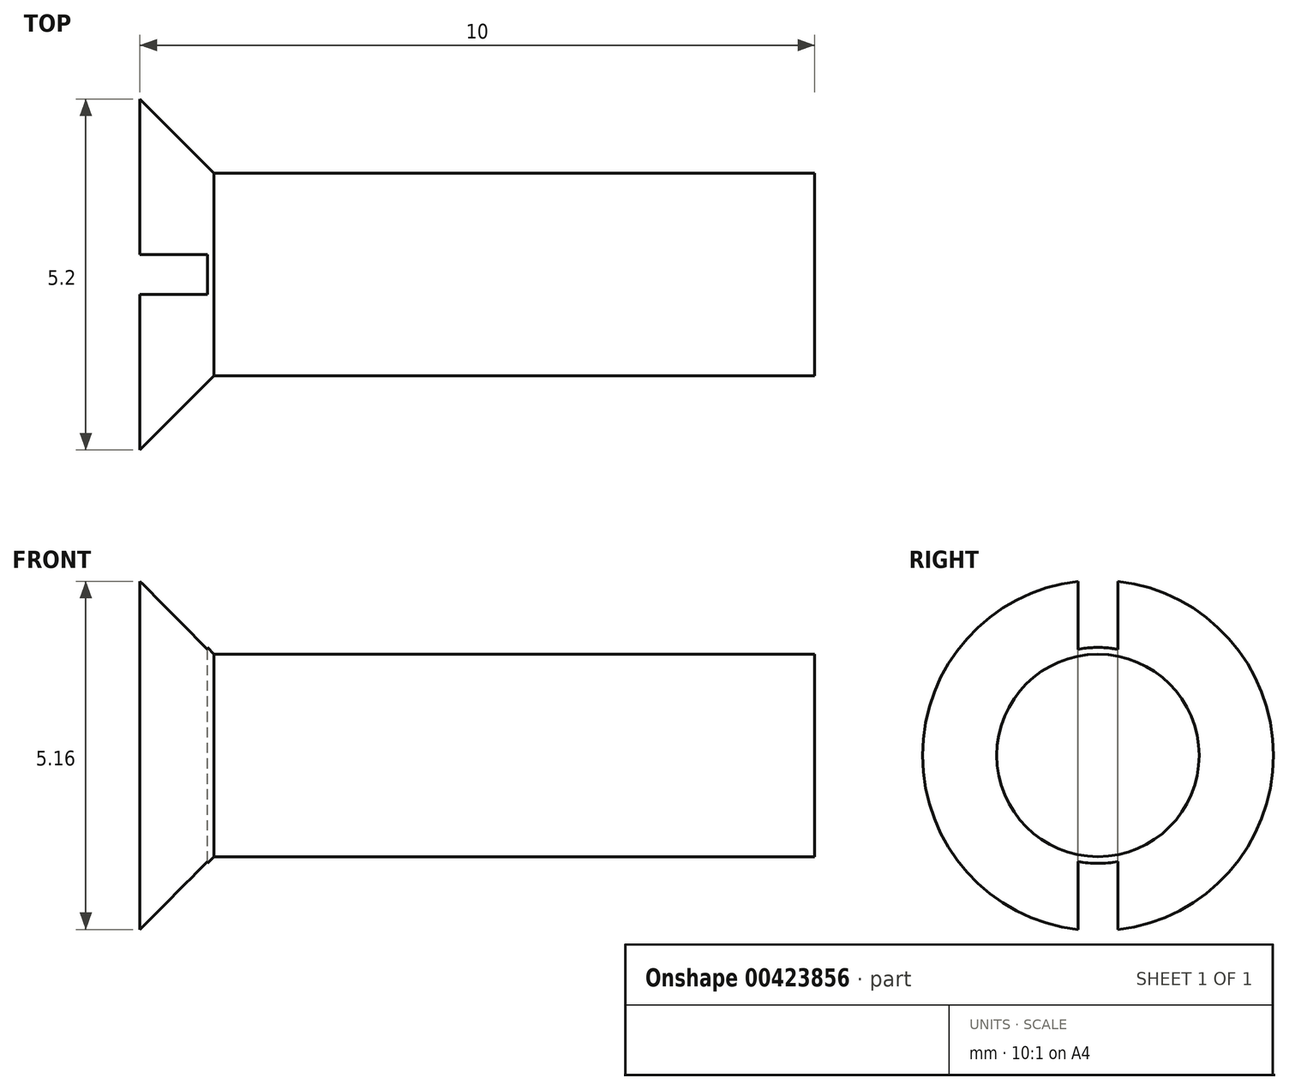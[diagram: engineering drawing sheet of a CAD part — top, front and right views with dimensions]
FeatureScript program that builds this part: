
annotation { "Feature Type Name" : "Feature", "Feature Type Description" : "" }
export const myFeature = defineFeature(function(context is Context, id is Id, definition is map)
    precondition{}
    {
        {
            var Q0;
            Q0=qCreatedBy(makeId("Front.planeOp"),FACE);
            var sketch = newSketch(context, id + "F0", { "sketchPlane" : qUnion([Q0])});
            skLineSegment(sketch, "E0", {"start": v(0, 0) * mm, "end": v(0, 2.6) * mm});
            skLineSegment(sketch, "E1", {"start": v(0, 2.6) * mm, "end": v(1.1, 1.5) * mm});
            skLineSegment(sketch, "E2", {"start": v(1.1, 1.5) * mm, "end": v(10, 1.5) * mm});
            skLineSegment(sketch, "E3", {"start": v(10, 1.5) * mm, "end": v(10, 0) * mm});
            skLineSegment(sketch, "E4", {"start": v(10, 0) * mm, "end": v(0, 0) * mm});
            skSolve(sketch);
        }
        {
            var Q0;
            Q0=qSketchRegion(id+"F0",true);
            var Q1;
            Q1=sQuery(id+"F0.wireOp",EDGE,"E4");
            revolve(context, id + "F1", {"entities" : qUnion([Q0]), "axis" : qUnion([Q1]), "revolveType" : RevolveType.FULL});
        }
        {
            var Q0;
            Q0=makeQuery(id+"F1.opRevolve","SWEPT_FACE",FACE,{"disambiguationData":[OSD([sQuery(id+"F0.wireOp",EDGE,"E0")])]});
            var sketch = newSketch(context, id + "F2", { "sketchPlane" : qUnion([Q0])});
            skLineSegment(sketch, "E5.bottom", {"start": v(0.3, -3.04) * mm, "end": v(-0.3, -3.04) * mm});
            skLineSegment(sketch, "E5.top", {"start": v(0.3, 3.04) * mm, "end": v(-0.3, 3.04) * mm});
            skLineSegment(sketch, "E5.left", {"start": v(0.3, -3.04) * mm, "end": v(0.3, 3.04) * mm});
            skLineSegment(sketch, "E5.right", {"start": v(-0.3, -3.04) * mm, "end": v(-0.3, 3.04) * mm});
            skPoint(sketch, "E5.middle", {"position": v(0, 0) * mm});
            skSolve(sketch);
        }
        {
            var Q0;
            Q0=qSketchRegion(id+"F2",true);
            extrude(context, id + "F3", {"entities" : qUnion([Q0]), "operationType" : NewBodyOperationType.REMOVE, "oppositeDirection" : true, "depth" : 1 * mm});
        }
    });
